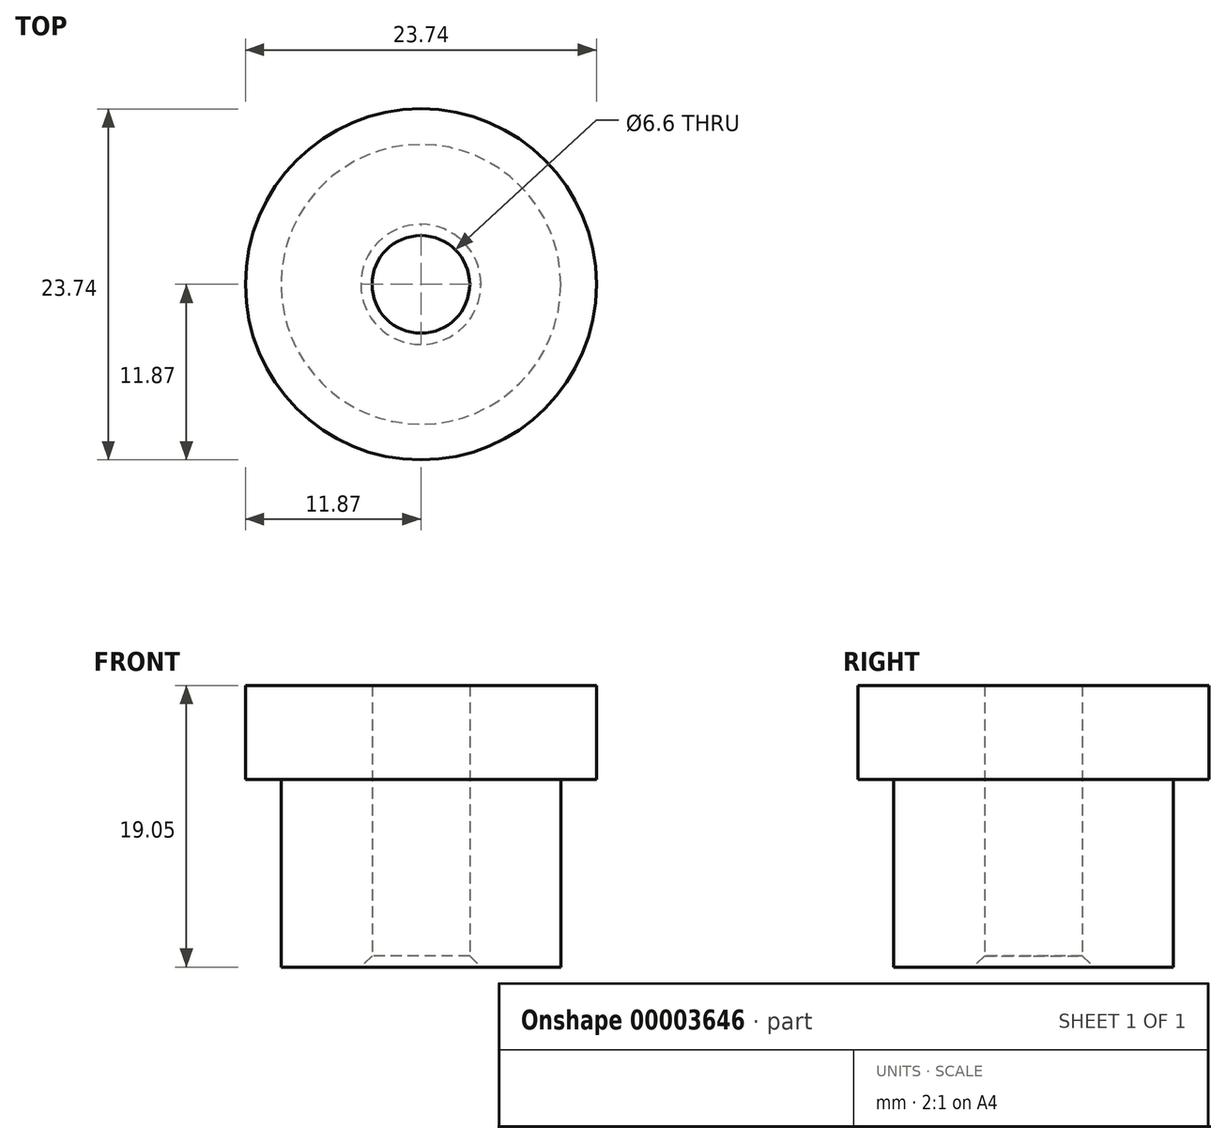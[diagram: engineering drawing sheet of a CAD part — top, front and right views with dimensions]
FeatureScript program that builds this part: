
annotation { "Feature Type Name" : "Feature", "Feature Type Description" : "" }
export const myFeature = defineFeature(function(context is Context, id is Id, definition is map)
    precondition{}
    {
        {
            var Q0;
            Q0=qCreatedBy(makeId("Top.planeOp"),FACE);
            var sketch = newSketch(context, id + "F0", { "sketchPlane" : qUnion([Q0])});
            skCircle(sketch, "E0", {"center": v(0, 0) * mm, "radius": 11.87 * mm});
            skCircle(sketch, "E1", {"center": v(0, 0) * mm, "radius": 3.3 * mm});
            skSolve(sketch);
        }
        {
            var Q0;
            Q0=qSketchRegion(id+"F0",true);
            extrude(context, id + "F1", {"entities" : qUnion([Q0]), "depth" : 19.05 * mm});
        }
        {
            var Q0;
            Q0=makeQuery(id+"F1.opExtrude","CAP_FACE",FACE,{"disambiguationData":[OSD([sQuery(id+"F0.wireOp",EDGE,"E0"),sQuery(id+"F0.wireOp",EDGE,"E1")])],"isStart":true});
            var sketch = newSketch(context, id + "F2", { "sketchPlane" : qUnion([Q0])});
            skCircle(sketch, "E2", {"center": v(0, 0) * mm, "radius": 9.46 * mm});
            skCircle(sketch, "E3.0", {"center": v(0, 0) * mm, "radius": 11.87 * mm});
            skSolve(sketch);
        }
        {
            var Q0;
            Q0=makeQuery(id+"F2.imprint","IMPRINT",FACE,{"disambiguationData":[TD([[makeQuery(id+"F2.imprint","IMPRINT",EDGE,{"derivedFrom":sQuery(id+"F2.wireOp",EDGE,"E2")}),-1.0]])]});
            extrude(context, id + "F3", {"entities" : qUnion([Q0]), "operationType" : NewBodyOperationType.REMOVE, "oppositeDirection" : true, "depth" : 12.7 * mm});
        }
        {
            var Q0;
            Q0=makeQuery(id+"F1.opExtrude","CAP_FACE",FACE,{"disambiguationData":[OSD([sQuery(id+"F0.wireOp",EDGE,"E0"),sQuery(id+"F0.wireOp",EDGE,"E1")])],"isStart":false});
            var sketch = newSketch(context, id + "F4", { "sketchPlane" : qUnion([Q0])});
            skCircle(sketch, "E4", {"center": v(0, 0) * mm, "radius": 7.5 * mm});
            skCircle(sketch, "E5.0", {"center": v(0, 0) * mm, "radius": 3.3 * mm});
            skSolve(sketch);
        }
        {
            var Q0;
            Q0=makeQuery(id+"FTdBSlmrk7DEJ0O_1.opExtrude","CAP_EDGE",EDGE,{"disambiguationData":[OSD([sQuery(id+"F4.wireOp",EDGE,"E5.0")])],"isStart":false});
            var Q1;
            Q1=makeQuery(id+"F1.opExtrude","CAP_EDGE",EDGE,{"disambiguationData":[OSD([sQuery(id+"F0.wireOp",EDGE,"E1")])],"isStart":true});
            chamfer(context, id + "F5", {"entities" : qUnion([Q0, Q1]), "width" : 0.76 * mm, "tangentPropagation" : true});
        }
    });
